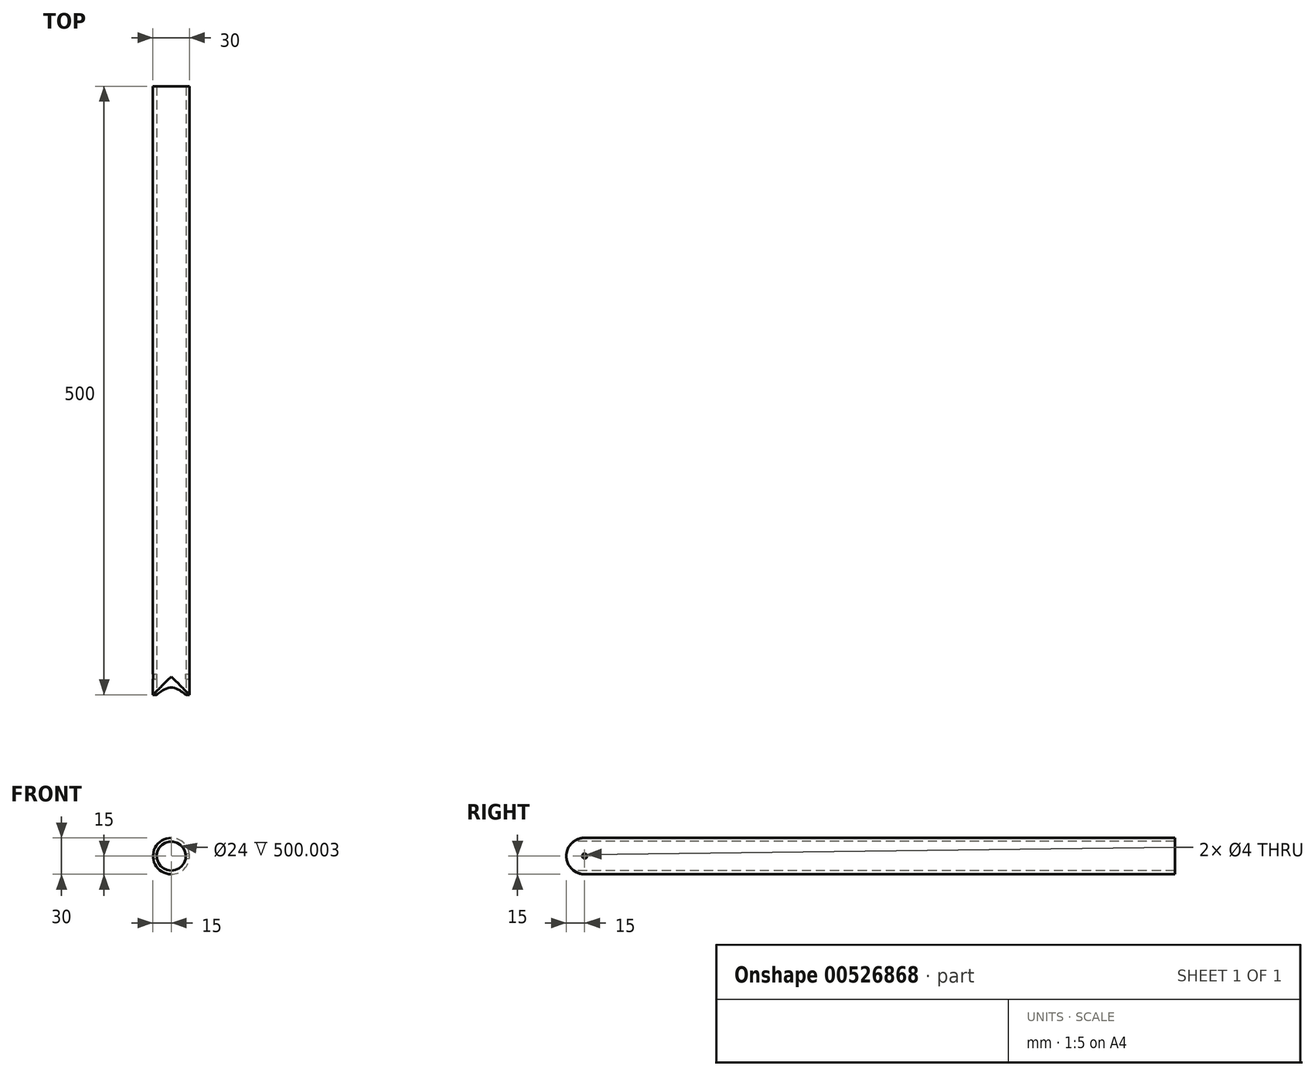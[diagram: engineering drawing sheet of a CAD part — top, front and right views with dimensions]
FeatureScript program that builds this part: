
annotation { "Feature Type Name" : "Feature", "Feature Type Description" : "" }
export const myFeature = defineFeature(function(context is Context, id is Id, definition is map)
    precondition{}
    {
        {
            var Q0;
            Q0=qCreatedBy(makeId("Front.planeOp"),FACE);
            var sketch = newSketch(context, id + "F0", { "sketchPlane" : qUnion([Q0])});
            skCircle(sketch, "E0", {"center": v(0, 0) * mm, "radius": 15 * mm});
            skCircle(sketch, "E1", {"center": v(0, 0) * mm, "radius": 12 * mm});
            skSolve(sketch);
        }
        {
            var Q0;
            Q0=makeQuery(id+"F0.imprint","IMPRINT",FACE,{"disambiguationData":[TD([[makeQuery(id+"F0.imprint","IMPRINT",EDGE,{"derivedFrom":sQuery(id+"F0.wireOp",EDGE,"E0")}),1.0]])]});
            extrude(context, id + "F1", {"entities" : qUnion([Q0]), "oppositeDirection" : true, "depth" : 500 * mm, "offsetDistance" : 25 * mm});
        }
        {
            var Q0;
            Q0=qCreatedBy(makeId("Right.planeOp"),FACE);
            var sketch = newSketch(context, id + "F2", { "sketchPlane" : qUnion([Q0])});
            skArc(sketch, "E2", {"start": v(15, 15) * mm, "mid": v(0, 0) * mm, "end": v(15, -15) * mm});
            skLineSegment(sketch, "E3", {"start": v(15, 15) * mm, "end": v(15, 24.67) * mm});
            skLineSegment(sketch, "E4", {"start": v(15, 24.67) * mm, "end": v(-7.86, 24.67) * mm});
            skLineSegment(sketch, "E5", {"start": v(-7.86, 24.67) * mm, "end": v(-7.86, -22.33) * mm});
            skLineSegment(sketch, "E6", {"start": v(-7.86, -22.33) * mm, "end": v(15, -22.33) * mm});
            skLineSegment(sketch, "E7", {"start": v(15, -22.33) * mm, "end": v(15, -15) * mm});
            skCircle(sketch, "E8", {"center": v(15, 0) * mm, "radius": 2 * mm});
            skSolve(sketch);
        }
        {
            var Q0;
            Q0=makeQuery(id+"F2.imprint","IMPRINT",FACE,{"disambiguationData":[TD([[makeQuery(id+"F2.imprint","IMPRINT",EDGE,{"derivedFrom":sQuery(id+"F2.wireOp",EDGE,"E2")}),-1.0]])]});
            var Q1;
            Q1=makeQuery(id+"F2.imprint","IMPRINT",FACE,{"disambiguationData":[TD([[makeQuery(id+"F2.imprint","IMPRINT",EDGE,{"derivedFrom":sQuery(id+"F2.wireOp",EDGE,"E8")}),1.0]])]});
            extrude(context, id + "F3", {"entities" : qUnion([Q0, Q1]), "operationType" : NewBodyOperationType.REMOVE, "oppositeDirection" : true, "depth" : 25 * mm, "offsetDistance" : 25 * mm, "hasSecondDirection" : true, "secondDirectionOppositeDirection" : false, "secondDirectionDepth" : 25 * mm});
        }
    });
